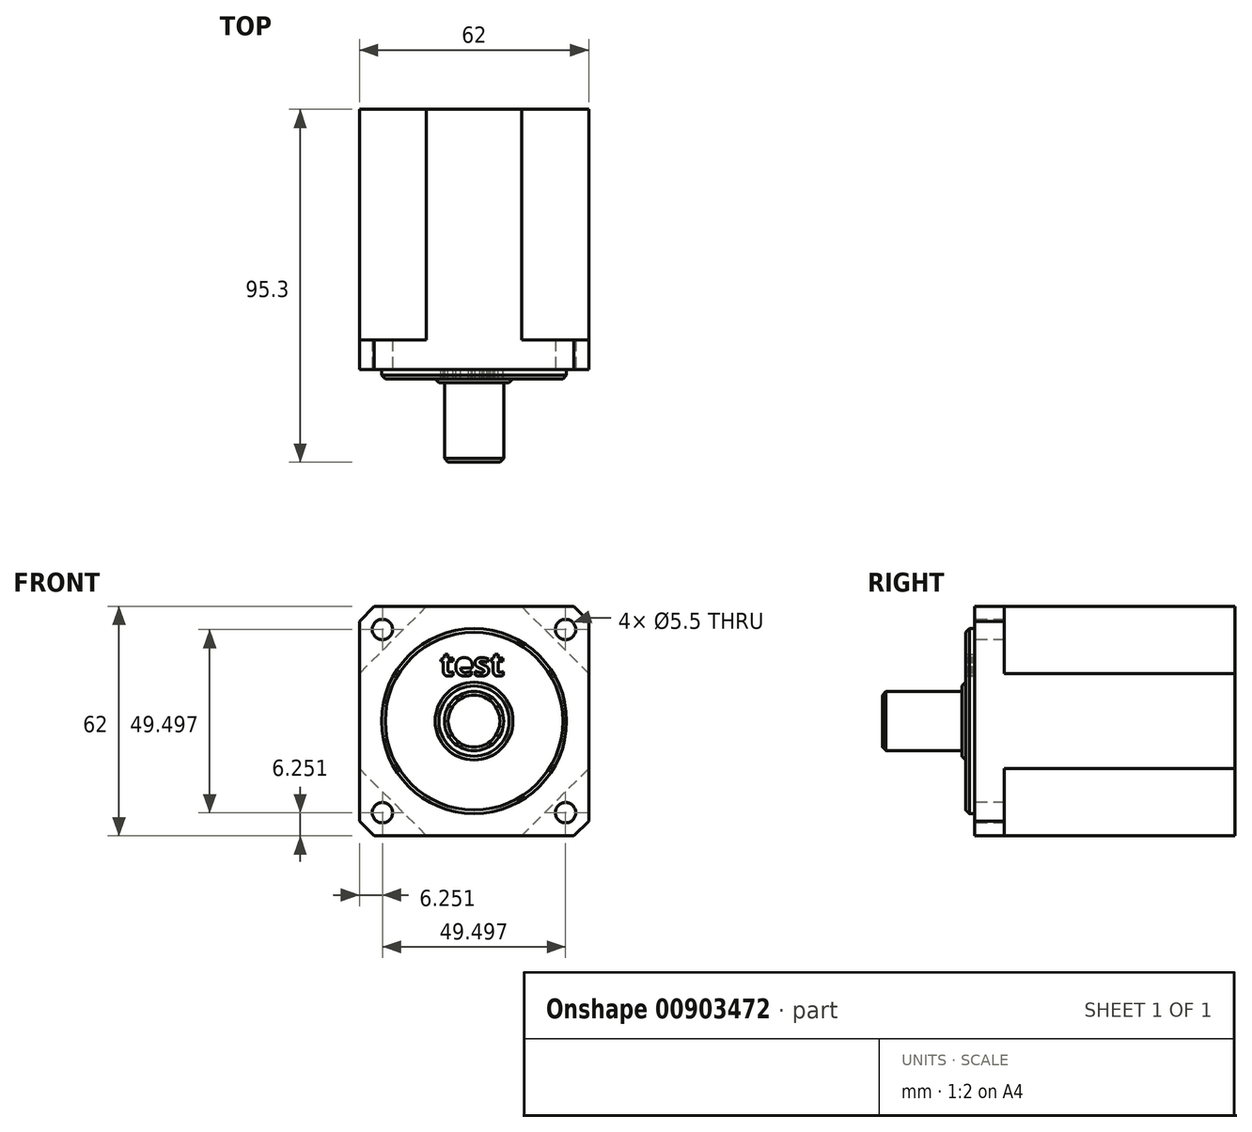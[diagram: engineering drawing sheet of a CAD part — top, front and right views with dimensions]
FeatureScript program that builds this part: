
annotation { "Feature Type Name" : "Feature", "Feature Type Description" : "" }
export const myFeature = defineFeature(function(context is Context, id is Id, definition is map)
    precondition{}
    {
        {
            var Q0;
            Q0=qCreatedBy(makeId("Front.planeOp"),FACE);
            var sketch = newSketch(context, id + "F0", { "sketchPlane" : qUnion([Q0])});
            skLineSegment(sketch, "E0.bottom", {"start": v(31, -31) * mm, "end": v(-31, -31) * mm});
            skLineSegment(sketch, "E0.top", {"start": v(31, 31) * mm, "end": v(-31, 31) * mm});
            skLineSegment(sketch, "E0.left", {"start": v(31, -31) * mm, "end": v(31, 31) * mm});
            skLineSegment(sketch, "E0.right", {"start": v(-31, -31) * mm, "end": v(-31, 31) * mm});
            skPoint(sketch, "E0.middle", {"position": v(0, 0) * mm});
            skLineSegment(sketch, "E1", {"start": v(12.84, 31) * mm, "end": v(31, 12.84) * mm});
            skLineSegment(sketch, "E2.1.0", {"start": v(-31, 12.84) * mm, "end": v(-12.84, 31) * mm});
            skLineSegment(sketch, "E2.2.0", {"start": v(-12.84, -31) * mm, "end": v(-31, -12.84) * mm});
            skLineSegment(sketch, "E2.3.0", {"start": v(31, -12.84) * mm, "end": v(12.84, -31) * mm});
            skSolve(sketch);
        }
        {
            var Q0;
            Q0=makeQuery(id+"F0.imprint","IMPRINT",FACE,{"disambiguationData":[TD([[makeQuery(id+"F0.imprint","IMPRINT",EDGE,{"derivedFrom":sQuery(id+"F0.wireOp",EDGE,"E0.bottom")}),-1.0]])]});
            var Q1;
            {var subQ3=sQuery(id+"F0.wireOp",EDGE,"E1");Q1=makeQuery(id+"F0.imprint","IMPRINT",FACE,{"disambiguationData":[TD([[makeQuery(id+"F0.imprint","IMPRINT",EDGE,{"derivedFrom":subQ3}),1.0]])]});}
            var Q2;
            {var subQ3=sQuery(id+"F0.wireOp",EDGE,"E1");Q2=makeQuery(id+"F0.imprint","IMPRINT",FACE,{"disambiguationData":[TD([[makeQuery(id+"F0.imprint","IMPRINT",EDGE,{"derivedFrom":subQ3}),-1.0]])]});}
            var Q3;
            {var subQ3=sQuery(id+"F0.wireOp",EDGE,"E2.1.0");Q3=makeQuery(id+"F0.imprint","IMPRINT",FACE,{"disambiguationData":[TD([[makeQuery(id+"F0.imprint","IMPRINT",EDGE,{"derivedFrom":subQ3}),1.0]])]});}
            extrude(context, id + "F1", {"entities" : qUnion([Q0, Q1, Q2, Q3]), "depth" : 70.3 * mm, "offsetDistance" : 25 * mm});
        }
        {
            var Q0;
            {var subQ3=sQuery(id+"F0.wireOp",EDGE,"E1");Q0=makeQuery(id+"F0.imprint","IMPRINT",FACE,{"disambiguationData":[TD([[makeQuery(id+"F0.imprint","IMPRINT",EDGE,{"derivedFrom":subQ3}),1.0]])]});}
            extrude(context, id + "F2", {"entities" : qUnion([Q0]), "operationType" : NewBodyOperationType.REMOVE, "depth" : 62.3 * mm, "offsetDistance" : 25 * mm});
        }
        {
            var Q0;
            {var subQ3=sQuery(id+"F0.wireOp",EDGE,"E2.1.0");Q0=makeQuery(id+"F0.imprint","IMPRINT",FACE,{"disambiguationData":[TD([[makeQuery(id+"F0.imprint","IMPRINT",EDGE,{"derivedFrom":subQ3}),1.0]])]});}
            var Q1;
            {var subQ3=sQuery(id+"F0.wireOp",EDGE,"E2.2.0");Q1=makeQuery(id+"F0.imprint","IMPRINT",FACE,{"disambiguationData":[TD([[makeQuery(id+"F0.imprint","IMPRINT",EDGE,{"derivedFrom":subQ3}),1.0]])]});}
            var Q2;
            {var subQ3=sQuery(id+"F0.wireOp",EDGE,"E2.3.0");Q2=makeQuery(id+"F0.imprint","IMPRINT",FACE,{"disambiguationData":[TD([[makeQuery(id+"F0.imprint","IMPRINT",EDGE,{"derivedFrom":subQ3}),1.0]])]});}
            extrude(context, id + "F3", {"entities" : qUnion([Q0, Q1, Q2]), "operationType" : NewBodyOperationType.REMOVE, "depth" : 62.3 * mm, "offsetDistance" : 25 * mm});
        }
        {
            var Q0;
            Q0=makeQuery(id+"F1.opExtrude","CAP_FACE",FACE,{"disambiguationData":[OSD([sQuery(id+"F0.wireOp",EDGE,"E0.bottom"),sQuery(id+"F0.wireOp",EDGE,"E0.top"),sQuery(id+"F0.wireOp",EDGE,"E0.left"),sQuery(id+"F0.wireOp",EDGE,"E0.right")])],"isStart":false});
            var sketch = newSketch(context, id + "F4", { "sketchPlane" : qUnion([Q0])});
            skCircle(sketch, "E3", {"center": v(0, 0) * mm, "radius": 35 * mm, "construction": true});
            skLineSegment(sketch, "E4", {"start": v(-31, 31) * mm, "end": v(31, -31) * mm, "construction": true});
            skLineSegment(sketch, "E5", {"start": v(31, 31) * mm, "end": v(-31, -31) * mm, "construction": true});
            skCircle(sketch, "E6", {"center": v(-24.75, 24.75) * mm, "radius": 2.75 * mm});
            skCircle(sketch, "E7", {"center": v(24.75, 24.75) * mm, "radius": 2.75 * mm});
            skCircle(sketch, "E8", {"center": v(24.75, -24.75) * mm, "radius": 2.75 * mm});
            skCircle(sketch, "E9", {"center": v(-24.75, -24.75) * mm, "radius": 2.75 * mm});
            skCircle(sketch, "E10", {"center": v(0, 0) * mm, "radius": 25 * mm});
            skCircle(sketch, "E11", {"center": v(0, 0) * mm, "radius": 41 * mm, "construction": true});
            skLineSegment(sketch, "E12", {"start": v(29, 29) * mm, "end": v(31, 26.98) * mm});
            skLineSegment(sketch, "E13", {"start": v(29, 29) * mm, "end": v(26.98, 31) * mm});
            skLineSegment(sketch, "E14.1.0", {"start": v(-29, 29) * mm, "end": v(-31, 26.98) * mm});
            skLineSegment(sketch, "E14.1.1", {"start": v(-29, 29) * mm, "end": v(-26.98, 31) * mm});
            skLineSegment(sketch, "E14.2.0", {"start": v(-29, -29) * mm, "end": v(-26.98, -31) * mm});
            skLineSegment(sketch, "E14.2.1", {"start": v(-29, -29) * mm, "end": v(-31, -26.98) * mm});
            skLineSegment(sketch, "E14.3.0", {"start": v(29, -29) * mm, "end": v(31, -26.98) * mm});
            skLineSegment(sketch, "E14.3.1", {"start": v(29, -29) * mm, "end": v(26.98, -31) * mm});
            skCircle(sketch, "E15", {"center": v(0, 0) * mm, "radius": 8 * mm});
            skText(sketch, "E16", { "text": "test", "fontName": "OpenSans-Bold.ttf"});
            const initialGuessF4  = {"E16": [-0.00917, 0.01223, 1, 0, 0.00638]};
            skSetInitialGuess(sketch, initialGuessF4);
            skSolve(sketch);
        }
        {
            var Q0;
            Q0=makeQuery(id+"F4.imprint","IMPRINT",FACE,{"disambiguationData":[TD([[makeQuery(id+"F4.imprint","IMPRINT",EDGE,{"derivedFrom":sQuery(id+"F4.wireOp",EDGE,"E6")}),1.0]])]});
            var Q1;
            Q1=makeQuery(id+"F4.imprint","IMPRINT",FACE,{"disambiguationData":[TD([[makeQuery(id+"F4.imprint","IMPRINT",EDGE,{"derivedFrom":sQuery(id+"F4.wireOp",EDGE,"E7")}),1.0]])]});
            var Q2;
            Q2=makeQuery(id+"F4.imprint","IMPRINT",FACE,{"disambiguationData":[TD([[makeQuery(id+"F4.imprint","IMPRINT",EDGE,{"derivedFrom":sQuery(id+"F4.wireOp",EDGE,"E8")}),1.0]])]});
            var Q3;
            Q3=makeQuery(id+"F4.imprint","IMPRINT",FACE,{"disambiguationData":[TD([[makeQuery(id+"F4.imprint","IMPRINT",EDGE,{"derivedFrom":sQuery(id+"F4.wireOp",EDGE,"E9")}),1.0]])]});
            extrude(context, id + "F5", {"entities" : qUnion([Q0, Q1, Q2, Q3]), "operationType" : NewBodyOperationType.REMOVE, "oppositeDirection" : true, "depth" : 8 * mm, "offsetDistance" : 25 * mm});
        }
        {
            var Q0;
            Q0=makeQuery(id+"F4.imprint","IMPRINT",FACE,{"disambiguationData":[TD([[makeQuery(id+"F4.imprint","IMPRINT",EDGE,{"derivedFrom":sQuery(id+"F4.wireOp",EDGE,"E10")}),1.0]])]});
            extrude(context, id + "F6", {"entities" : qUnion([Q0]), "operationType" : NewBodyOperationType.ADD, "depth" : 2.5 * mm, "offsetDistance" : 25 * mm});
        }
        {
            var Q0;
            {var subQ0=sQuery(id+"F4.wireOp",EDGE,"E12");Q0=makeQuery(id+"F4.imprint","IMPRINT",FACE,{"disambiguationData":[TD([[makeQuery(id+"F4.imprint","IMPRINT",EDGE,{"derivedFrom":subQ0}),1.0]])]});}
            var Q1;
            {var subQ0=sQuery(id+"F4.wireOp",EDGE,"E14.3.0");Q1=makeQuery(id+"F4.imprint","IMPRINT",FACE,{"disambiguationData":[TD([[makeQuery(id+"F4.imprint","IMPRINT",EDGE,{"derivedFrom":subQ0}),-1.0]])]});}
            var Q2;
            {var subQ0=sQuery(id+"F4.wireOp",EDGE,"E14.2.0");Q2=makeQuery(id+"F4.imprint","IMPRINT",FACE,{"disambiguationData":[TD([[makeQuery(id+"F4.imprint","IMPRINT",EDGE,{"derivedFrom":subQ0}),-1.0]])]});}
            var Q3;
            {var subQ0=sQuery(id+"F4.wireOp",EDGE,"E14.1.0");Q3=makeQuery(id+"F4.imprint","IMPRINT",FACE,{"disambiguationData":[TD([[makeQuery(id+"F4.imprint","IMPRINT",EDGE,{"derivedFrom":subQ0}),-1.0]])]});}
            extrude(context, id + "F7", {"entities" : qUnion([Q0, Q1, Q2, Q3]), "operationType" : NewBodyOperationType.REMOVE, "endBound" : BoundingType.THROUGH_ALL, "oppositeDirection" : true, "depth" : 32 * mm, "offsetDistance" : 25 * mm});
        }
        {
            var Q0;
            Q0=makeQuery(id+"F6.opExtrude","CAP_FACE",FACE,{"disambiguationData":[OSD([sQuery(id+"F4.wireOp",EDGE,"E10")])],"isStart":false});
            var sketch = newSketch(context, id + "F8", { "sketchPlane" : qUnion([Q0])});
            skCircle(sketch, "E17", {"center": v(0, 0) * mm, "radius": 10.5 * mm});
            skSolve(sketch);
        }
        {
            var Q0;
            Q0=makeQuery(id+"F8.imprint","IMPRINT",FACE,{"disambiguationData":[TD([[makeQuery(id+"F8.imprint","IMPRINT",EDGE,{"derivedFrom":sQuery(id+"F8.wireOp",EDGE,"E17")}),1.0]])]});
            extrude(context, id + "F9", {"entities" : qUnion([Q0]), "operationType" : NewBodyOperationType.ADD, "depth" : 1 * mm, "offsetDistance" : 25 * mm});
        }
        {
            var Q0;
            Q0=makeQuery(id+"F9.opExtrude","CAP_EDGE",EDGE,{"disambiguationData":[OSD([sQuery(id+"F8.wireOp",EDGE,"E17")])],"isStart":false});
            chamfer(context, id + "F10", {"entities" : qUnion([Q0]), "width" : 1 * mm, "tangentPropagation" : true});
        }
        {
            var Q0;
            Q0=makeQuery(id+"F6.opExtrude","CAP_EDGE",EDGE,{"disambiguationData":[OSD([sQuery(id+"F4.wireOp",EDGE,"E10")])],"isStart":false});
            chamfer(context, id + "F11", {"entities" : qUnion([Q0]), "width" : 1 * mm, "tangentPropagation" : true});
        }
        {
            var Q0;
            Q0=makeQuery(id+"F4.imprint","IMPRINT",FACE,{"disambiguationData":[TD([[makeQuery(id+"F4.imprint","IMPRINT",EDGE,{"derivedFrom":sQuery(id+"F4.wireOp",EDGE,"E15")}),1.0]])]});
            extrude(context, id + "F12", {"entities" : qUnion([Q0]), "operationType" : NewBodyOperationType.ADD, "depth" : 25 * mm, "offsetDistance" : 25 * mm});
        }
        {
            var Q0;
            Q0=makeQuery(id+"F12.opExtrude","CAP_EDGE",EDGE,{"disambiguationData":[OSD([sQuery(id+"F4.wireOp",EDGE,"E15")])],"isStart":false});
            chamfer(context, id + "F13", {"entities" : qUnion([Q0]), "width" : 1 * mm, "tangentPropagation" : true});
        }
    });
